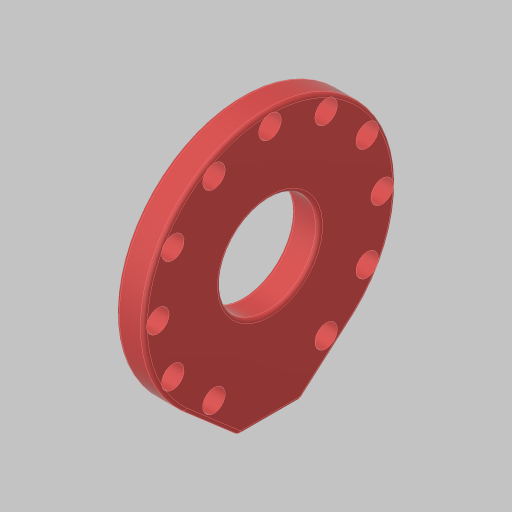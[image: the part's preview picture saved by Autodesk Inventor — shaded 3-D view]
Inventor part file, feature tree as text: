
AUTODESK INVENTOR PART (.ipt)
format: ipt  version: 2023.5 (Build 275446000, 446)  size: 218,624 bytes
history: native  units: in
note: dims shown in document units (in); Inventor stores cm internally (conversion verified against a paired STEP export)
features: sketch x1, extrude x1, hole x1, fillet x1
ambient origin geometry x8: Origin, YZ Plane, XZ Plane, XY Plane, X Axis, Y Axis, Z Axis, Center Point
bodies: Solid1 (feature_tree)
feature tree (4):
  sketch  "Sketch1"  dims[d0=2.25in d1=1.25in d4=0.645in d5=0.55in d7=2.0in d8=4.7244in d10=360.0deg d12=0.25in d13=0.0in d14=0.201in d15=0.432in d16=0.375in d17=0.25in d18=0.5635in d19=1.0in d20=0.8108in d21=0.0312in d22=0.875in]
  extrude  "Extrusion1"  Depth=0.0312in
  hole  "Hole1"  [1 undecoded]
  fillet  "Fillet1"  Radius=0.55in
note: 1 required parameter value undecoded (feature->parameter linkage not recoverable at this tier; creation-order binding heuristic only, values carry confidence <= 0.55)
